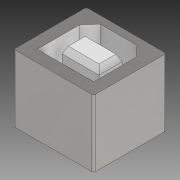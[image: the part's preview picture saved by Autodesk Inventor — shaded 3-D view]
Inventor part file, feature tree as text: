
AUTODESK INVENTOR PART (.ipt)
format: ipt  version: 2016 (Build 200138000, 138)  size: 182,272 bytes
history: native  units: mm
features: sketch x6, extrude x5, fillet x1, projected_geometry x1
ambient origin geometry x8: Origin, YZ Plane, XZ Plane, XY Plane, X Axis, Y Axis, Z Axis, Center Point
bodies: Solid1 (feature_tree)
feature tree (13):
  sketch  "Sketch1"  dims[d0=9.11mm d1=0.0mm d2=1.0mm d3=0.0mm]
  extrude  "Extrusion1"  Depth=1.0mm TaperAngle=0.0deg
  extrude  "Extrusion2"  Depth=1.0mm
  extrude  "Extrusion3"  Depth=0.3mm
  extrude  "Extrusion4"  [1 undecoded]
  extrude  "Extrusion5"  [1 undecoded]
  fillet  "Fillet1"  [1 undecoded]
  sketch  "Sketch2"  dims[d4=8.11mm d5=0.0mm d6=1.0mm d7=-4.363323mm]
  sketch  "Sketch3"  dims[d8=6.84mm d9=0.0mm d10=0.3mm]
  sketch  "Sketch4"
  sketch  "Sketch5"
  projected_geometry  "Projected Loop1"
  sketch  "Sketch6"
note: 3 required parameter values undecoded (feature->parameter linkage not recoverable at this tier; creation-order binding heuristic only, values carry confidence <= 0.55)
